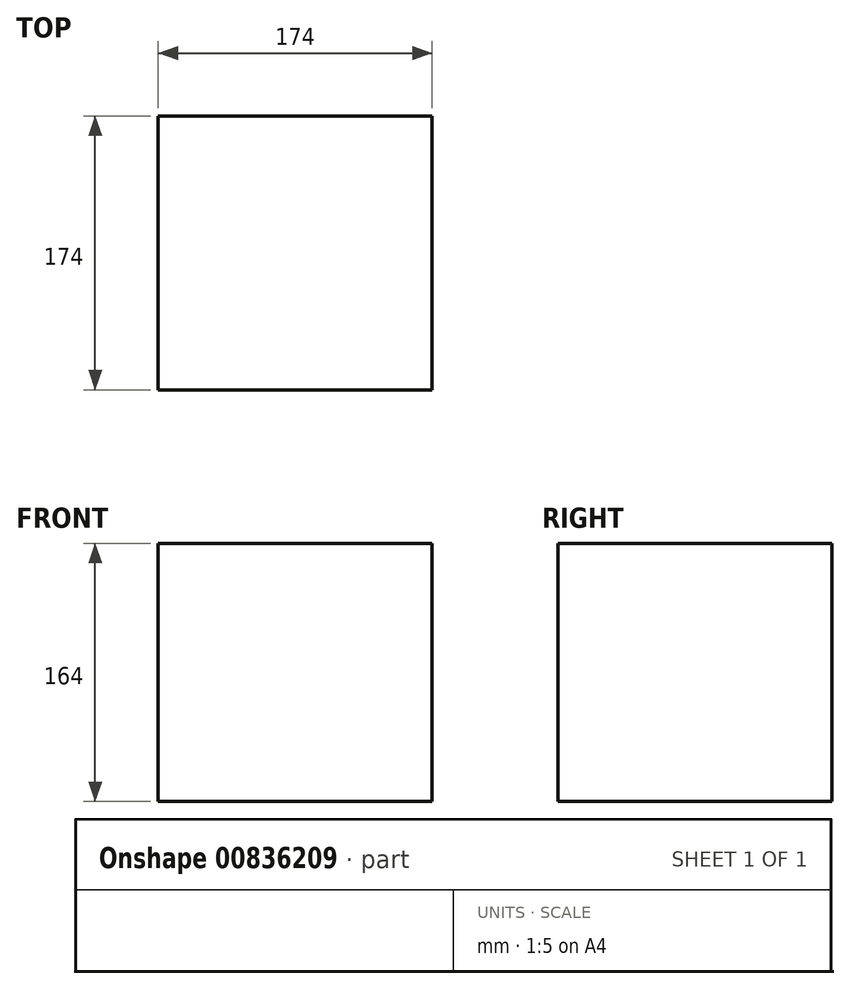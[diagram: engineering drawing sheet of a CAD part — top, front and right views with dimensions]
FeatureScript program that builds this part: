
annotation { "Feature Type Name" : "Feature", "Feature Type Description" : "" }
export const myFeature = defineFeature(function(context is Context, id is Id, definition is map)
    precondition{}
    {
        {
            var Q0;
            Q0=qCreatedBy(makeId("Top.planeOp"),FACE);
            var sketch = newSketch(context, id + "F0", { "sketchPlane" : qUnion([Q0])});
            skLineSegment(sketch, "E0.bottom", {"start": v(0, 0) * mm, "end": v(174, 0) * mm});
            skLineSegment(sketch, "E0.top", {"start": v(0, -174) * mm, "end": v(174, -174) * mm});
            skLineSegment(sketch, "E0.left", {"start": v(0, 0) * mm, "end": v(0, -174) * mm});
            skLineSegment(sketch, "E0.right", {"start": v(174, 0) * mm, "end": v(174, -174) * mm});
            skSolve(sketch);
        }
        {
            var Q0;
            Q0=makeQuery(id+"F0.imprint","IMPRINT",FACE,{"disambiguationData":[TD([[makeQuery(id+"F0.imprint","IMPRINT",EDGE,{"derivedFrom":sQuery(id+"F0.wireOp",EDGE,"E0.bottom")}),-1.0]])]});
            extrude(context, id + "F1", {"entities" : qUnion([Q0]), "depth" : 164 * mm, "offsetDistance" : 25 * mm});
        }
    });
